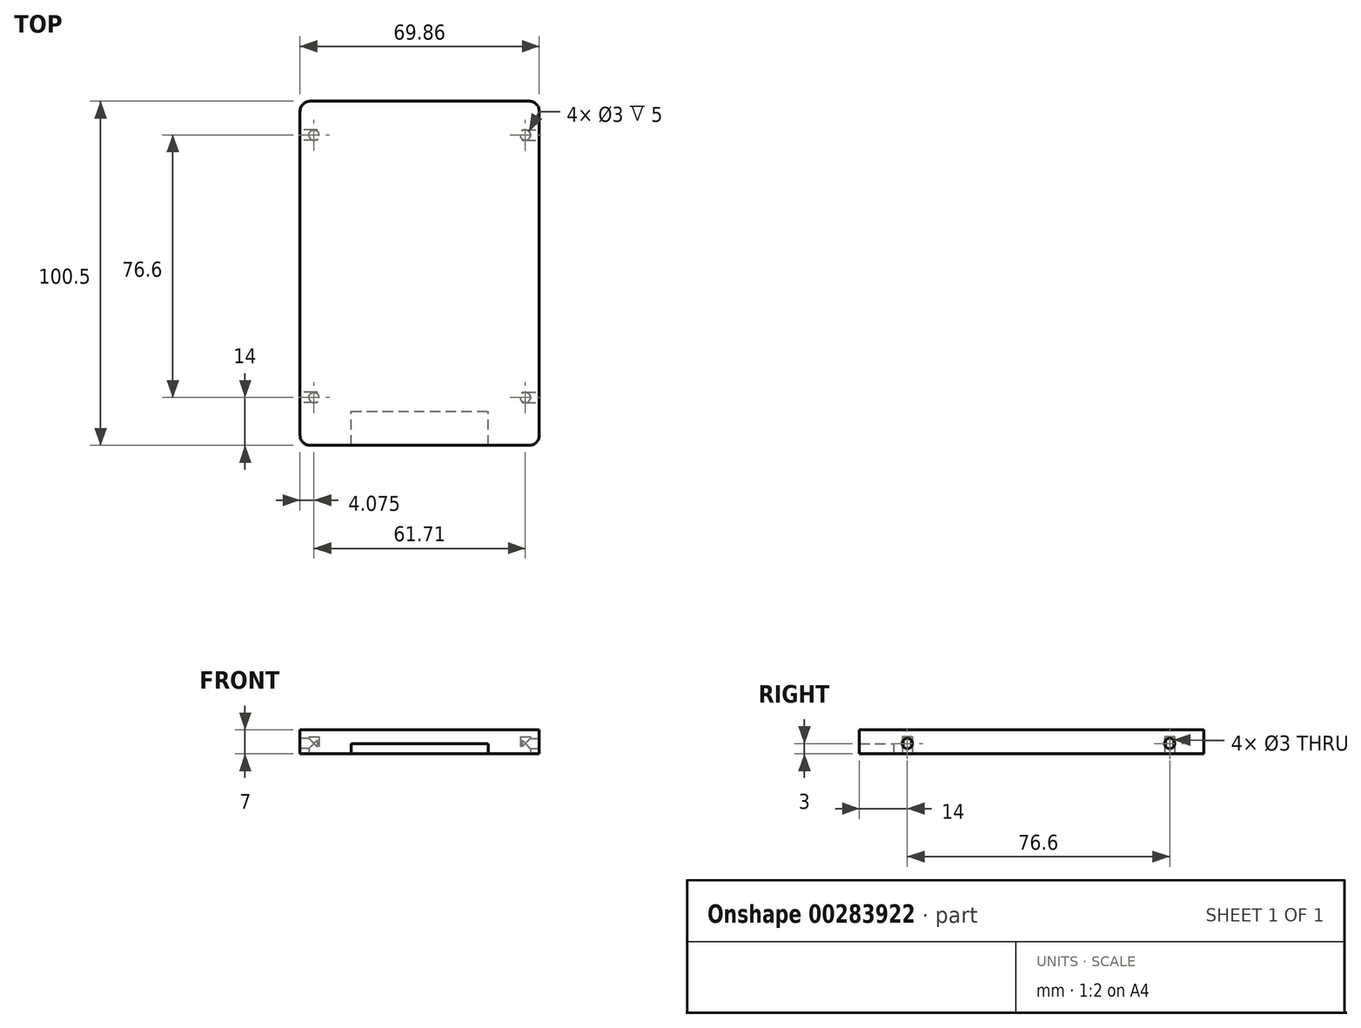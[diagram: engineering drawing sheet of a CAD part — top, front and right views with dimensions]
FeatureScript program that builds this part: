
annotation { "Feature Type Name" : "Feature", "Feature Type Description" : "" }
export const myFeature = defineFeature(function(context is Context, id is Id, definition is map)
    precondition{}
    {
        {
            var Q0;
            Q0=qCreatedBy(makeId("Top.planeOp"),FACE);
            var sketch = newSketch(context, id + "F0", { "sketchPlane" : qUnion([Q0])});
            skLineSegment(sketch, "E0.bottom", {"start": v(34.92, 50.25) * mm, "end": v(-34.93, 50.25) * mm});
            skLineSegment(sketch, "E0.top", {"start": v(34.93, -50.25) * mm, "end": v(-34.92, -50.25) * mm});
            skLineSegment(sketch, "E0.left", {"start": v(34.92, 50.25) * mm, "end": v(34.93, -50.25) * mm});
            skLineSegment(sketch, "E0.right", {"start": v(-34.93, 50.25) * mm, "end": v(-34.92, -50.25) * mm});
            skPoint(sketch, "E0.middle", {"position": v(0, 0) * mm});
            skSolve(sketch);
        }
        {
            var Q0;
            Q0 = qSketchRegion(id + "F0", true);
            extrude(context, id + "F1", {"entities" : qUnion([Q0]), "depth" : 7 * mm});
        }
        {
            var Q0;
            Q0=makeQuery(id+"F1.opExtrude","SWEPT_EDGE",EDGE,{"disambiguationData":[OSD([sQuery(id+"F0.wireOp",EDGE,"E0.bottom"),sQuery(id+"F0.wireOp",EDGE,"E0.left")])]});
            var Q1;
            Q1=makeQuery(id+"F1.opExtrude","SWEPT_EDGE",EDGE,{"disambiguationData":[OSD([sQuery(id+"F0.wireOp",EDGE,"E0.bottom"),sQuery(id+"F0.wireOp",EDGE,"E0.right")])]});
            var Q2;
            Q2=makeQuery(id+"F1.opExtrude","SWEPT_EDGE",EDGE,{"disambiguationData":[OSD([sQuery(id+"F0.wireOp",EDGE,"E0.top"),sQuery(id+"F0.wireOp",EDGE,"E0.left")])]});
            var Q3;
            Q3=makeQuery(id+"F1.opExtrude","SWEPT_EDGE",EDGE,{"disambiguationData":[OSD([sQuery(id+"F0.wireOp",EDGE,"E0.top"),sQuery(id+"F0.wireOp",EDGE,"E0.right")])]});
            fillet(context, id + "F2", {"entities" : qUnion([Q0, Q1, Q2, Q3]), "radius" : 3 * mm, "tangentPropagation" : true, "allowEdgeOverflow" : false});
        }
        {
            var Q0;
            Q0=makeQuery(id+"F1.opExtrude","SWEPT_FACE",FACE,{"disambiguationData":[OSD([sQuery(id+"F0.wireOp",EDGE,"E0.left")])]});
            var sketch = newSketch(context, id + "F3", { "sketchPlane" : qUnion([Q0])});
            skCircle(sketch, "E1", {"center": v(-36.25, 3) * mm, "radius": 1.5 * mm});
            skCircle(sketch, "E2", {"center": v(40.35, 3) * mm, "radius": 1.5 * mm});
            skSolve(sketch);
        }
        {
            var Q0;
            Q0 = qSketchRegion(id + "F3", true);
            extrude(context, id + "F4", {"entities" : qUnion([Q0]), "operationType" : NewBodyOperationType.REMOVE, "oppositeDirection" : true, "depth" : 5 * mm});
        }
        {
            var Q0;
            Q0=makeQuery(id+"F1.opExtrude","SWEPT_FACE",FACE,{"disambiguationData":[OSD([sQuery(id+"F0.wireOp",EDGE,"E0.right")])]});
            var sketch = newSketch(context, id + "F5", { "sketchPlane" : qUnion([Q0])});
            skCircle(sketch, "E3.0", {"center": v(36.25, 3) * mm, "radius": 1.5 * mm});
            skCircle(sketch, "E3.1", {"center": v(-40.35, 3) * mm, "radius": 1.5 * mm});
            skSolve(sketch);
        }
        {
            var Q0;
            Q0 = qSketchRegion(id + "F5", true);
            extrude(context, id + "F6", {"entities" : qUnion([Q0]), "operationType" : NewBodyOperationType.REMOVE, "oppositeDirection" : true, "depth" : 5 * mm});
        }
        {
            var Q0;
            Q0=makeQuery(id+"F1.opExtrude","CAP_FACE",FACE,{"disambiguationData":[OSD([sQuery(id+"F0.wireOp",EDGE,"E0.bottom"),sQuery(id+"F0.wireOp",EDGE,"E0.top"),sQuery(id+"F0.wireOp",EDGE,"E0.left"),sQuery(id+"F0.wireOp",EDGE,"E0.right")])],"isStart":true});
            var sketch = newSketch(context, id + "F7", { "sketchPlane" : qUnion([Q0])});
            skLineSegment(sketch, "E4.bottom", {"start": v(-20, 50.25) * mm, "end": v(20, 50.25) * mm});
            skLineSegment(sketch, "E4.top", {"start": v(-20, 40.25) * mm, "end": v(20, 40.25) * mm});
            skLineSegment(sketch, "E4.left", {"start": v(-20, 50.25) * mm, "end": v(-20, 40.25) * mm});
            skLineSegment(sketch, "E4.right", {"start": v(20, 50.25) * mm, "end": v(20, 40.25) * mm});
            skPoint(sketch, "E5", {"position": v(0, 50.25) * mm});
            skSolve(sketch);
        }
        {
            var Q0;
            Q0 = qSketchRegion(id + "F7", true);
            extrude(context, id + "F8", {"entities" : qUnion([Q0]), "operationType" : NewBodyOperationType.REMOVE, "oppositeDirection" : true, "depth" : 3 * mm});
        }
        {
            var Q0;
            Q0=makeQuery(id+"F1.opExtrude","CAP_FACE",FACE,{"disambiguationData":[OSD([sQuery(id+"F0.wireOp",EDGE,"E0.bottom"),sQuery(id+"F0.wireOp",EDGE,"E0.top"),sQuery(id+"F0.wireOp",EDGE,"E0.left"),sQuery(id+"F0.wireOp",EDGE,"E0.right")])],"isStart":true});
            var sketch = newSketch(context, id + "F9", { "sketchPlane" : qUnion([Q0])});
            skCircle(sketch, "E6", {"center": v(-30.86, 36.25) * mm, "radius": 1.5 * mm});
            skCircle(sketch, "E7", {"center": v(-30.85, -40.35) * mm, "radius": 1.5 * mm});
            skLineSegment(sketch, "E8", {"start": v(0, 0) * mm, "end": v(0, -44.37) * mm, "construction": true});
            skCircle(sketch, "E9.MirrorC", {"center": v(30.85, -40.35) * mm, "radius": 1.5 * mm});
            skCircle(sketch, "E10.MirrorC", {"center": v(30.86, 36.25) * mm, "radius": 1.5 * mm});
            skSolve(sketch);
        }
        {
            var Q0;
            Q0 = qSketchRegion(id + "F9", true);
            extrude(context, id + "F10", {"entities" : qUnion([Q0]), "operationType" : NewBodyOperationType.REMOVE, "oppositeDirection" : true, "depth" : 5 * mm});
        }
    });
